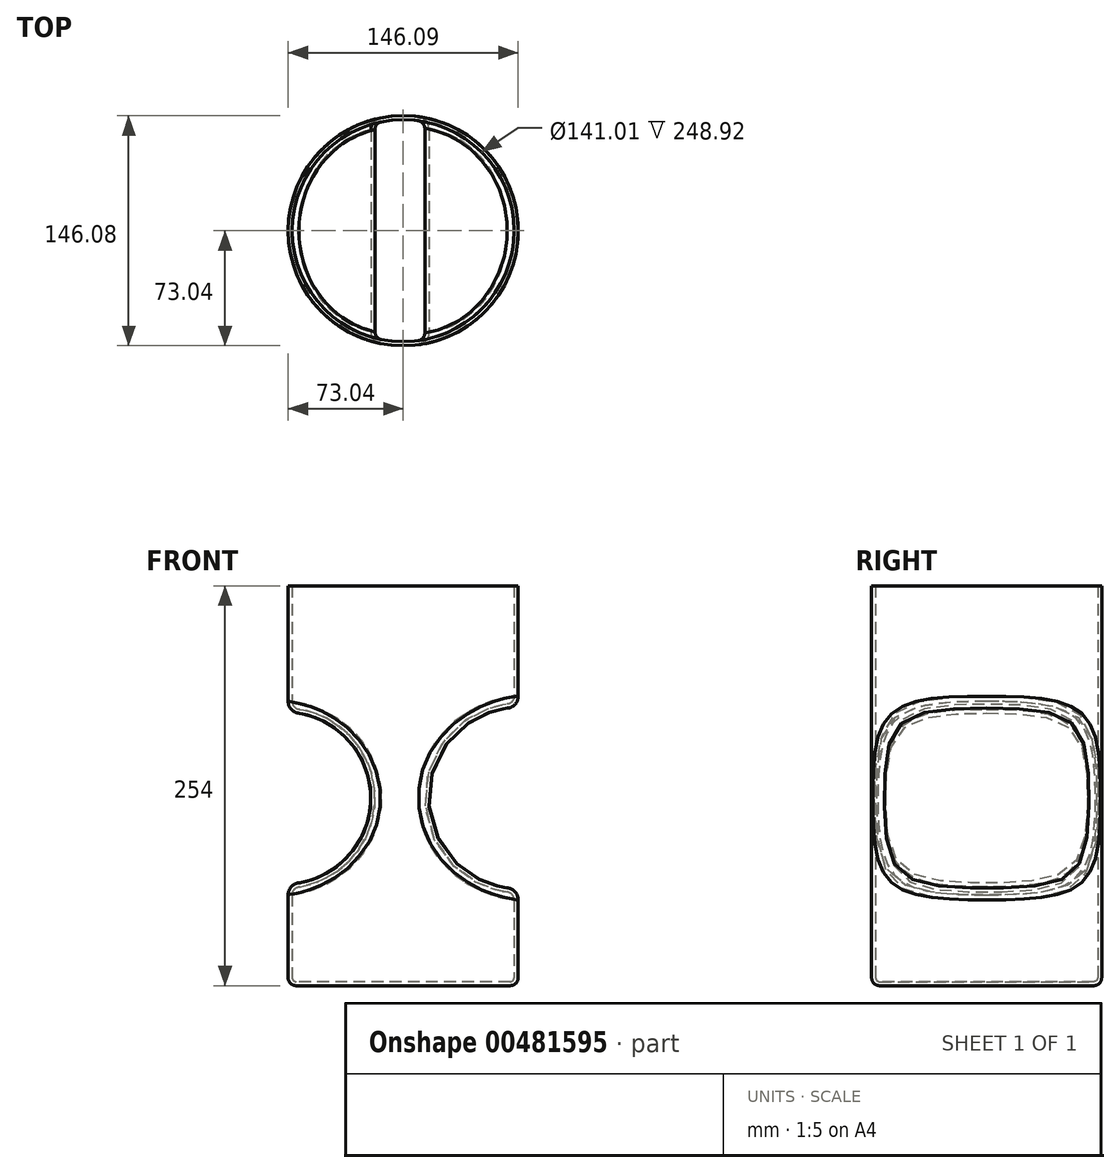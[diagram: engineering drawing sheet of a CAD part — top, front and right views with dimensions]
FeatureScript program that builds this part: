
annotation { "Feature Type Name" : "Feature", "Feature Type Description" : "" }
export const myFeature = defineFeature(function(context is Context, id is Id, definition is map)
    precondition{}
    {
        {
            var Q0;
            Q0=qCreatedBy(makeId("Top.planeOp"),FACE);
            var sketch = newSketch(context, id + "F0", { "sketchPlane" : qUnion([Q0])});
            skCircle(sketch, "E0", {"center": v(0, 0) * mm, "radius": 73.04 * mm});
            skSolve(sketch);
        }
        {
            var Q0;
            Q0 = qSketchRegion(id + "F0", true);
            extrude(context, id + "F1", {"entities" : qUnion([Q0]), "depth" : 254 * mm});
        }
        {
            var Q0;
            Q0=qCreatedBy(makeId("Front.planeOp"),FACE);
            var sketch = newSketch(context, id + "F2", { "sketchPlane" : qUnion([Q0])});
            skCircle(sketch, "E1", {"center": v(-75.08, 119.17) * mm, "radius": 54.58 * mm});
            skCircle(sketch, "E2", {"center": v(73.89, 119.17) * mm, "radius": 57.6 * mm});
            skSolve(sketch);
        }
        {
            var Q0;
            Q0 = qSketchRegion(id + "F2", true);
            extrude(context, id + "F3", {"entities" : qUnion([Q0]), "operationType" : NewBodyOperationType.REMOVE, "endBound" : BoundingType.SYMMETRIC, "oppositeDirection" : true, "depth" : 254 * mm});
        }
        {
            var Q0;
            Q0=makeQuery(id+"F3.boolean.opBoolean","INTERSECT",EDGE,{"derivedFrom":[makeQuery(id+"F1.opExtrude","SWEPT_FACE",FACE,{"disambiguationData":[OSD([sQuery(id+"F0.wireOp",EDGE,"E0")])]}),makeQuery(id+"F3.opExtrude","SWEPT_FACE",FACE,{"disambiguationData":[OSD([sQuery(id+"F2.wireOp",EDGE,"E2")])]})]});
            var Q1;
            Q1=makeQuery(id+"F3.boolean.opBoolean","INTERSECT",EDGE,{"derivedFrom":[makeQuery(id+"F1.opExtrude","SWEPT_FACE",FACE,{"disambiguationData":[OSD([sQuery(id+"F0.wireOp",EDGE,"E0")])]}),makeQuery(id+"F3.opExtrude","SWEPT_FACE",FACE,{"disambiguationData":[OSD([sQuery(id+"F2.wireOp",EDGE,"E1")])]})]});
            fillet(context, id + "F4", {"entities" : qUnion([Q0, Q1]), "radius" : 7.62 * mm, "tangentPropagation" : true, "allowEdgeOverflow" : false});
        }
        {
            var Q0;
            Q0=makeQuery(id+"F1.opExtrude","CAP_EDGE",EDGE,{"disambiguationData":[OSD([sQuery(id+"F0.wireOp",EDGE,"E0")])],"isStart":true});
            fillet(context, id + "F5", {"entities" : qUnion([Q0]), "radius" : 5.08 * mm, "tangentPropagation" : true, "allowEdgeOverflow" : false});
        }
        {
            var Q0;
            Q0=makeQuery(id+"F1.opExtrude","CAP_FACE",FACE,{"disambiguationData":[OSD([sQuery(id+"F0.wireOp",EDGE,"E0")])],"isStart":false});
            shell(context, id + "F6", {"entities" : qUnion([Q0]), "thickness" : 2.54 * mm});
        }
    });
